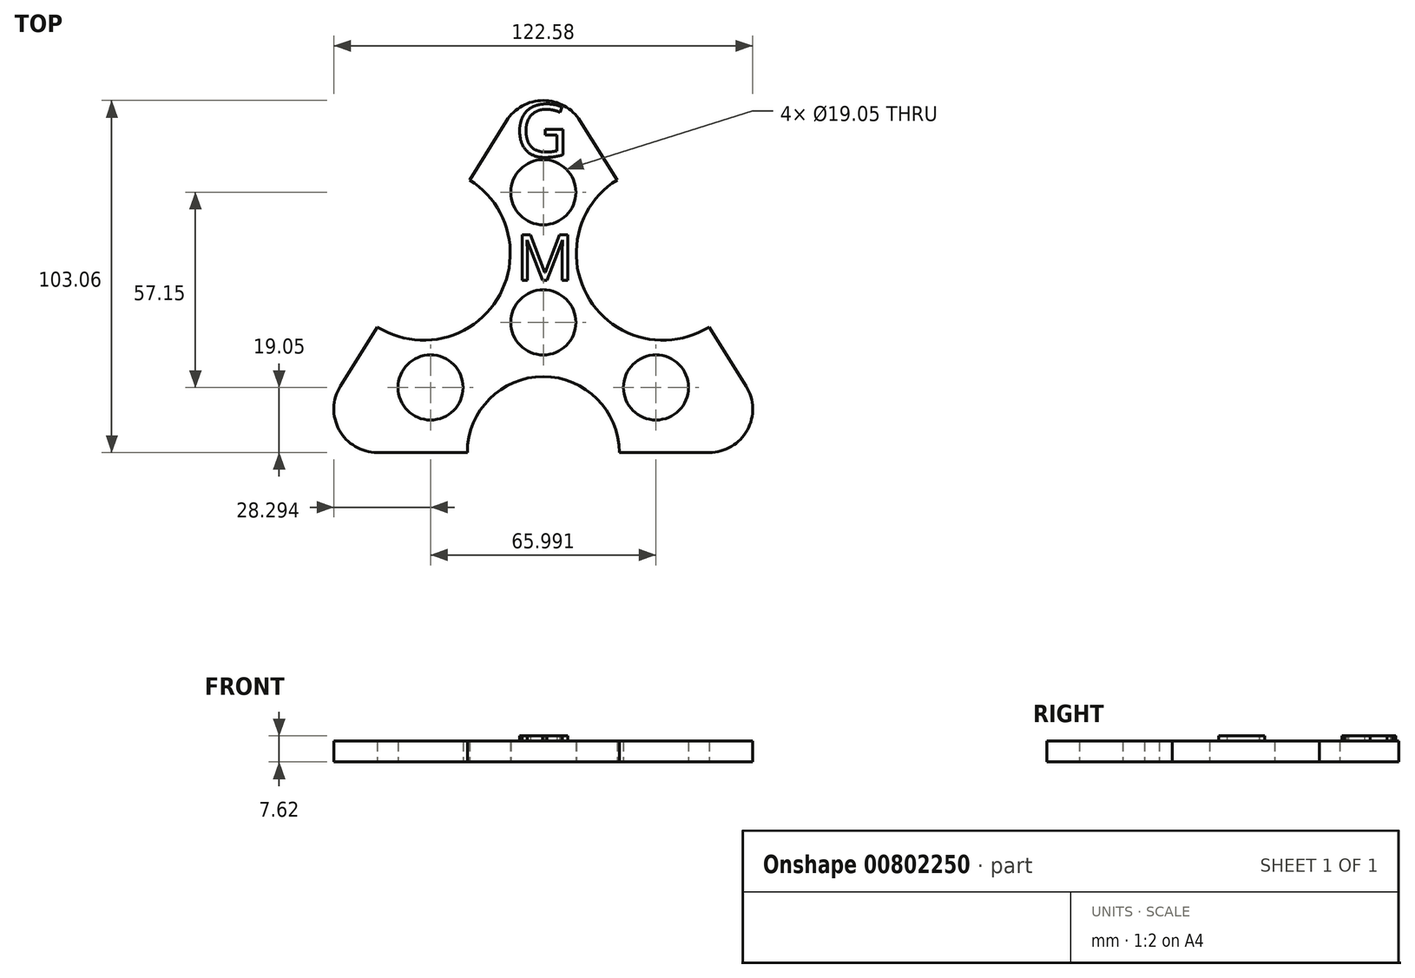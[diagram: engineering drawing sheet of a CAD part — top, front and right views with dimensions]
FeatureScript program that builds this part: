
annotation { "Feature Type Name" : "Feature", "Feature Type Description" : "" }
export const myFeature = defineFeature(function(context is Context, id is Id, definition is map)
    precondition{}
    {
        {
            var Q0;
            Q0=qCreatedBy(makeId("Top.planeOp"),FACE);
            var sketch = newSketch(context, id + "F0", { "sketchPlane" : qUnion([Q0])});
            skCircle(sketch, "E0", {"center": v(0, 38.1) * mm, "radius": 9.53 * mm});
            skCircle(sketch, "E1", {"center": v(-33, -19.05) * mm, "radius": 9.53 * mm});
            skCircle(sketch, "E2", {"center": v(0, 0) * mm, "radius": 9.53 * mm});
            skCircle(sketch, "E3.MirrorC", {"center": v(33, -19.05) * mm, "radius": 9.53 * mm});
            skLineSegment(sketch, "E4", {"start": v(0, 0) * mm, "end": v(0, 38.1) * mm});
            skLineSegment(sketch, "E5", {"start": v(0, 0) * mm, "end": v(33, -19.05) * mm});
            skLineSegment(sketch, "E6", {"start": v(-48.6, -38.1) * mm, "end": v(-22.23, -38.1) * mm});
            skLineSegment(sketch, "E7", {"start": v(0, 0) * mm, "end": v(-33, -19.05) * mm});
            skLineSegment(sketch, "E8", {"start": v(0, 0) * mm, "end": v(0, -38.1) * mm, "construction": true});
            skLineSegment(sketch, "E9", {"start": v(0, 38.1) * mm, "end": v(0, 76.2) * mm, "construction": true});
            skLineSegment(sketch, "E10", {"start": v(-10.77, 59) * mm, "end": v(-21.59, 41.7) * mm});
            skLineSegment(sketch, "E11", {"start": v(10.77, 59) * mm, "end": v(21.59, 41.7) * mm});
            skPoint(sketch, "E12.visualSharp", {"position": v(0, 76.2) * mm});
            skArc(sketch, "E12.filletArc", {"start": v(10.77, 59) * mm, "mid": v(0, 64.96) * mm, "end": v(-10.77, 59) * mm});
            skPoint(sketch, "E13.visualSharp", {"position": v(-71.52, -38.1) * mm});
            skArc(sketch, "E13.filletArc", {"start": v(-59.36, -18.66) * mm, "mid": v(-59.7, -31.55) * mm, "end": v(-48.6, -38.1) * mm});
            skPoint(sketch, "E14.visualSharp", {"position": v(71.52, -38.1) * mm});
            skArc(sketch, "E14.filletArc", {"start": v(48.6, -38.1) * mm, "mid": v(59.7, -31.55) * mm, "end": v(59.36, -18.66) * mm});
            skArc(sketch, "E15", {"start": v(-48.54, -1.37) * mm, "mid": v(-13.53, 6.7) * mm, "end": v(-21.59, 41.7) * mm});
            skArc(sketch, "E16.MirrorC", {"start": v(48.54, -1.37) * mm, "mid": v(13.53, 6.7) * mm, "end": v(21.59, 41.7) * mm});
            skArc(sketch, "E17", {"start": v(22.23, -38.1) * mm, "mid": v(0, -15.87) * mm, "end": v(-22.23, -38.1) * mm});
            skLineSegment(sketch, "E18.trimOffspring", {"start": v(48.54, -1.37) * mm, "end": v(59.36, -18.66) * mm});
            skLineSegment(sketch, "E19.trimOffspring", {"start": v(22.23, -38.1) * mm, "end": v(48.6, -38.1) * mm});
            skLineSegment(sketch, "E20.trimOffspring", {"start": v(-48.54, -1.37) * mm, "end": v(-59.36, -18.66) * mm});
            skSolve(sketch);
        }
        {
            var Q0;
            Q0 = qSketchRegion(id + "F0", true);
            extrude(context, id + "F1", {"entities" : qUnion([Q0]), "depth" : 6.1 * mm, "offsetDistance" : 25.4 * mm});
        }
        {
            var Q0;
            Q0=makeQuery(id+"F1.opExtrude","CAP_FACE",FACE,{"disambiguationData":[OSD([sQuery(id+"F0.wireOp",EDGE,"E0"),sQuery(id+"F0.wireOp",EDGE,"E1"),sQuery(id+"F0.wireOp",EDGE,"E2"),sQuery(id+"F0.wireOp",EDGE,"E3.MirrorC"),sQuery(id+"F0.wireOp",EDGE,"E6"),sQuery(id+"F0.wireOp",EDGE,"E10"),sQuery(id+"F0.wireOp",EDGE,"E11"),sQuery(id+"F0.wireOp",EDGE,"E12.filletArc"),sQuery(id+"F0.wireOp",EDGE,"E13.filletArc"),sQuery(id+"F0.wireOp",EDGE,"E14.filletArc"),sQuery(id+"F0.wireOp",EDGE,"E15"),sQuery(id+"F0.wireOp",EDGE,"E16.MirrorC"),sQuery(id+"F0.wireOp",EDGE,"E17"),sQuery(id+"F0.wireOp",EDGE,"E18.trimOffspring"),sQuery(id+"F0.wireOp",EDGE,"E19.trimOffspring"),sQuery(id+"F0.wireOp",EDGE,"E20.trimOffspring")])],"isStart":false});
            var sketch = newSketch(context, id + "F2", { "sketchPlane" : qUnion([Q0])});
            skText(sketch, "E21", { "text": "G", "fontName": "OpenSans-Regular.ttf"});
            skText(sketch, "E22", { "text": "M", "fontName": "OpenSans-Regular.ttf"});
            const initialGuessF2  = {"E21": [-0.00822, 0.0485, 1, 0, 0.01538], "E22": [-0.00796, 0.01225, 1, 0, 0.01347]};
            skSetInitialGuess(sketch, initialGuessF2);
            skSolve(sketch);
        }
        {
            var Q0;
            Q0 = qSketchRegion(id + "F2", true);
            extrude(context, id + "F3", {"entities" : qUnion([Q0]), "operationType" : NewBodyOperationType.ADD, "depth" : 1.52 * mm, "offsetDistance" : 25.4 * mm});
        }
    });
